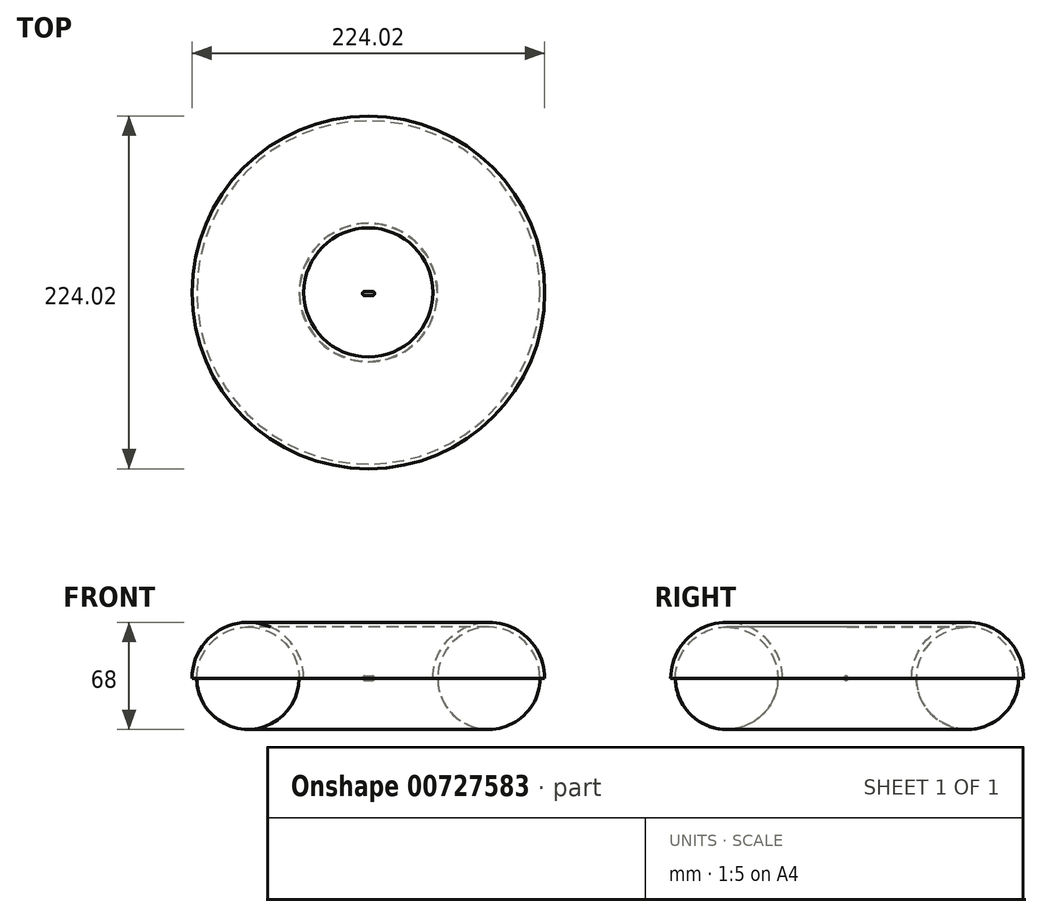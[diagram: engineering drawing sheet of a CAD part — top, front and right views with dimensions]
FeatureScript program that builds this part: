
annotation { "Feature Type Name" : "Feature", "Feature Type Description" : "" }
export const myFeature = defineFeature(function(context is Context, id is Id, definition is map)
    precondition{}
    {
        {
            var Q0;
            Q0=qCreatedBy(makeId("Front.planeOp"),FACE);
            var sketch = newSketch(context, id + "F0", { "sketchPlane" : qUnion([Q0])});
            skLineSegment(sketch, "E0", {"start": v(0, 180.24) * mm, "end": v(0, -197) * mm, "construction": true});
            skCircle(sketch, "E1", {"center": v(76.5, 0) * mm, "radius": 32.5 * mm});
            skArc(sketch, "E2", {"start": v(112, 0) * mm, "mid": v(76.5, 35.5) * mm, "end": v(41, 0) * mm});
            skLineSegment(sketch, "E3", {"start": v(41, 0) * mm, "end": v(44, 0) * mm});
            skLineSegment(sketch, "E4", {"start": v(109, 0) * mm, "end": v(112, 0) * mm});
            skSolve(sketch);
        }
        {
            var Q0;
            Q0=makeQuery(id+"F0.imprint","IMPRINT",FACE,{"disambiguationData":[TD([[makeQuery(id+"F0.imprint","IMPRINT",EDGE,{"derivedFrom":sQuery(id+"F0.wireOp",EDGE,"E1")}),1.0]])]});
            var Q1;
            Q1=sQuery(id+"F0.wireOp",EDGE,"E0");
            revolve(context, id + "F1", {"surfaceOperationType" : NewSurfaceOperationType.NEW, "entities" : qUnion([Q0]), "axis" : qUnion([Q1]), "revolveType" : RevolveType.FULL});
        }
        {
            var Q0;
            Q0 = qSketchRegion(id + "F0", true);
            var Q1;
            Q1=makeQuery(id+"F1.opRevolve","SWEPT_FACE",FACE,{"disambiguationData":[OSD([sQuery(id+"F0.wireOp",EDGE,"E1")])]});
            revolve(context, id + "F2", {"surfaceOperationType" : NewSurfaceOperationType.NEW, "entities" : qUnion([Q0]), "axis" : qUnion([Q1]), "revolveType" : RevolveType.FULL});
        }
        {
            var Q0;
            Q0=qCreatedBy(makeId("Top.planeOp"),FACE);
            var sketch = newSketch(context, id + "F3", { "sketchPlane" : qUnion([Q0])});
            skLineSegment(sketch, "E5.bottom", {"start": v(2.61, -1.98) * mm, "end": v(-2.39, -1.98) * mm});
            skArc(sketch, "E6", {"start": v(2.61, -1.98) * mm, "mid": v(3.55, -1.6) * mm, "end": v(3.93, -0.66) * mm});
            skArc(sketch, "E7", {"start": v(-3.7, -0.66) * mm, "mid": v(-3.32, -1.6) * mm, "end": v(-2.39, -1.98) * mm});
            skLineSegment(sketch, "E8", {"start": v(4.88, -0.66) * mm, "end": v(-4.44, -0.66) * mm, "construction": true});
            skLineSegment(sketch, "E9", {"start": v(3.93, -0.66) * mm, "end": v(-3.7, -0.66) * mm, "construction": true});
            skLineSegment(sketch, "E10", {"start": v(3.93, -0.66) * mm, "end": v(-3.7, -0.66) * mm});
            skSolve(sketch);
        }
        {
            var Q0;
            Q0=makeQuery(id+"F3.imprint","IMPRINT",FACE,{"disambiguationData":[TD([[makeQuery(id+"F3.imprint","IMPRINT",EDGE,{"derivedFrom":sQuery(id+"F3.wireOp",EDGE,"E5.bottom")}),-1.0]])]});
            var Q1;
            Q1=sQuery(id+"F3.wireOp",EDGE,"E8");
            revolve(context, id + "F4", {"surfaceOperationType" : NewSurfaceOperationType.NEW, "entities" : qUnion([Q0]), "axis" : qUnion([Q1]), "revolveType" : RevolveType.FULL});
        }
    });
